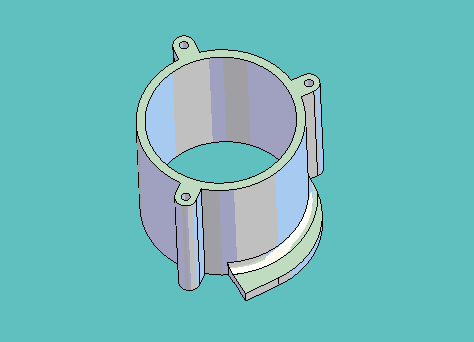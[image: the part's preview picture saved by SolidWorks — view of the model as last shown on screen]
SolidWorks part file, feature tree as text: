
SOLIDWORKS PART (.sldprt)
format: sldprt  version: not decoded by parser v0  size: 939,008 bytes
history: native  units: mm
features: sketch x7, extrude x4, fillet x4, cut_extrude x3, material x1, plane x1 (+11 scaffold rows collapsed)
feature tree (31):
  scaffold x11  (default folders/planes/origin — collapsed)
  material  "Material <not specified>"
  sketch  "Sketch1"  dims[c1.D1=46.355mm c1.D2=52.705mm c2.D1=~8.054899mm]
  extrude  "Extrude1"  Depth=3.175mm
  sketch  "Sketch2"  dims[D1=0.0mm]
  extrude  "Extrude2"  Depth=50.8mm
  fillet  "Fillet4"  Radius=3.175mm
  fillet  "Fillet5"  Radius=2.54mm
  fillet  "Fillet6"  Radius=2.54mm
  sketch  "Sketch4"
  extrude  "Extrude3"  Depth=4.7625mm
  fillet  "Fillet2"  Radius=3.175mm
  sketch  "Sketch6"  dims[D1=7.9375mm]
  cut_extrude  "Cut-Extrude2"  Depth=9.525mm
  sketch  "Sketch7"
  extrude  "Extrude5"  [1 undecoded]
  sketch  "Sketch8"  dims[c1.D3=3.175mm c1.D5=3.175mm c1.D7=3.175mm c1.D1=~37.608622mm c2.D1=120.0deg c2.D2=~44.89201mm c3.D2=120.0deg c3.D4=34.925mm c3.D6=34.925mm c3.D8=34.925mm c3.D1=~37.608622mm c4.D1=60.0deg c4.D2=~44.89201mm c5.D2=77.0deg c6.D2=~37.608622mm c7.D2=137.0deg c7.D9=~50.092853mm c8.D9=137.0deg]
  sketch  "Sketch9"  dims[c1.D3=3.175mm c1.D5=~2.38125mm c1.D7=3.175mm c1.D1=~37.608622mm c2.D1=120.0deg c2.D2=~44.89201mm c3.D2=120.0deg c3.D4=34.925mm c3.D6=34.925mm c3.D8=34.925mm c3.D1=~48.345797mm c4.D1=60.0deg c4.D2=~46.467312mm c5.D2=137.0deg c5.D9=~46.004503mm c6.D9=137.0deg]
  cut_extrude  "Cut-Extrude3"  Depth=9.525mm
  cut_extrude  "Cut-Extrude4"  Depth=9.525mm
  plane  "Plane2"
decode coverage: 15 of 18 modeling features carry decoded parameters
note: ~ marks probable driven/reference dimensions
note: 1 parameter value undecoded
note: suppression state not decoded; provenance and decode notes live in map.json
